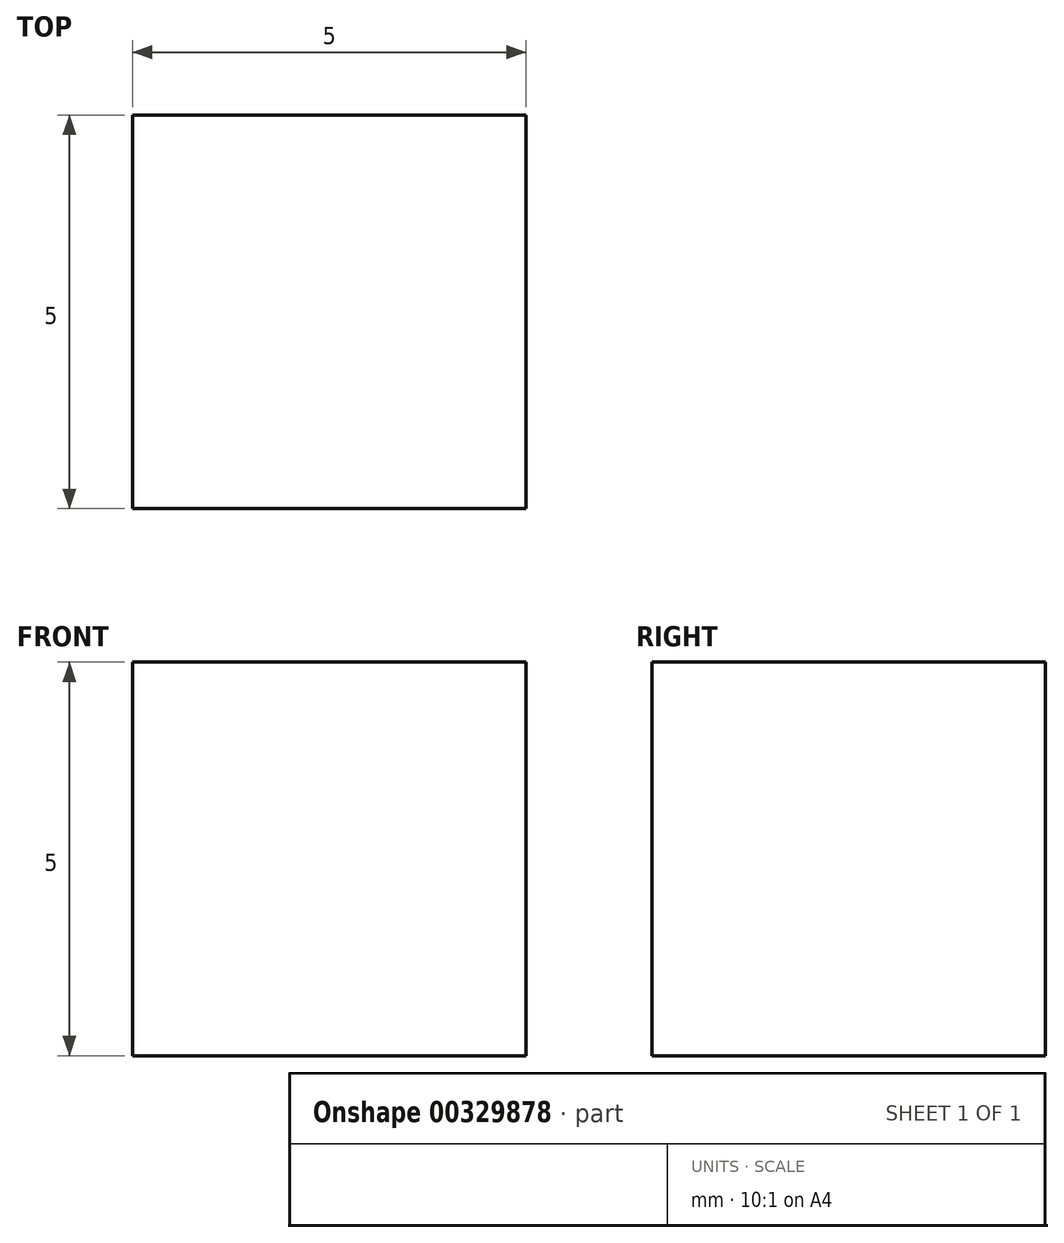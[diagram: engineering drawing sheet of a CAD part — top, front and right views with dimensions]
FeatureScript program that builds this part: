
annotation { "Feature Type Name" : "Feature", "Feature Type Description" : "" }
export const myFeature = defineFeature(function(context is Context, id is Id, definition is map)
    precondition{}
    {
        {
            assignVariable(context, id + "F0", {"variableType" : VariableType.LENGTH, "name" : "dim", "lengthValue" : 5 * mm});
        }
        {
            var Q0;
            Q0=qCreatedBy(makeId("Top.planeOp"),FACE);
            var sketch = newSketch(context, id + "F1", { "sketchPlane" : qUnion([Q0])});
            skLineSegment(sketch, "E0.bottom", {"start": v(0, 0) * mm, "end": v(5, 0) * mm});
            skLineSegment(sketch, "E0.top", {"start": v(0, 5) * mm, "end": v(5, 5) * mm});
            skLineSegment(sketch, "E0.left", {"start": v(0, 0) * mm, "end": v(0, 5) * mm});
            skLineSegment(sketch, "E0.right", {"start": v(5, 0) * mm, "end": v(5, 5) * mm});
            skSolve(sketch);
        }
        {
            var Q0;
            Q0 = qSketchRegion(id + "F1", true);
            extrude(context, id + "F2", {"entities" : qUnion([Q0]), "depth" : getVariable(context, 'dim'), "offsetDistance" : 25 * mm});
        }
    });
